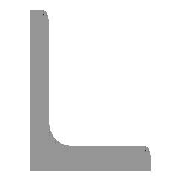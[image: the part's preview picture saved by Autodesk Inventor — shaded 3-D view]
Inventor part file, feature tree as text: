
AUTODESK INVENTOR PART (.ipt)
format: ipt  version: 2013 (Build 170138000, 138)  size: 130,048 bytes
history: native  units: mm (DEFAULTED — no unit token found)
features: other x4, plane x3, split x2, sketch x2
ambient origin geometry x8: Origin, YZ Plane, XZ Plane, XY Plane, X Axis, Y Axis, Z Axis, Center Point
bodies: Solid1 (feature_tree), Body (feature_tree)
feature tree (11):
  parser-record x1  (decoder bookkeeping rows leaked as tree rows — omitted from the tree; the rows remain in map.json)
  other  "Driven Length"
  other  "Start plane"
  other  "End plane"
  plane  "Work Plane4"
  split  "Split1"
  plane  "Work Plane5"
  split  "Split2"
  sketch  "Sketch3"  dims[d0=38.1mm]
  plane  "Work Plane3"
  sketch  "Sketch4"  dims[d1=38.1mm d2=4.7625mm d3=4.7625mm d4=1244.6mm d5=0.0mm d10=0.0mm d11=0.0mm d12=-0.0mm d13=1244.6mm d14=4.826mm d15=2.286mm d16=90.0deg d17=1244.6mm]
